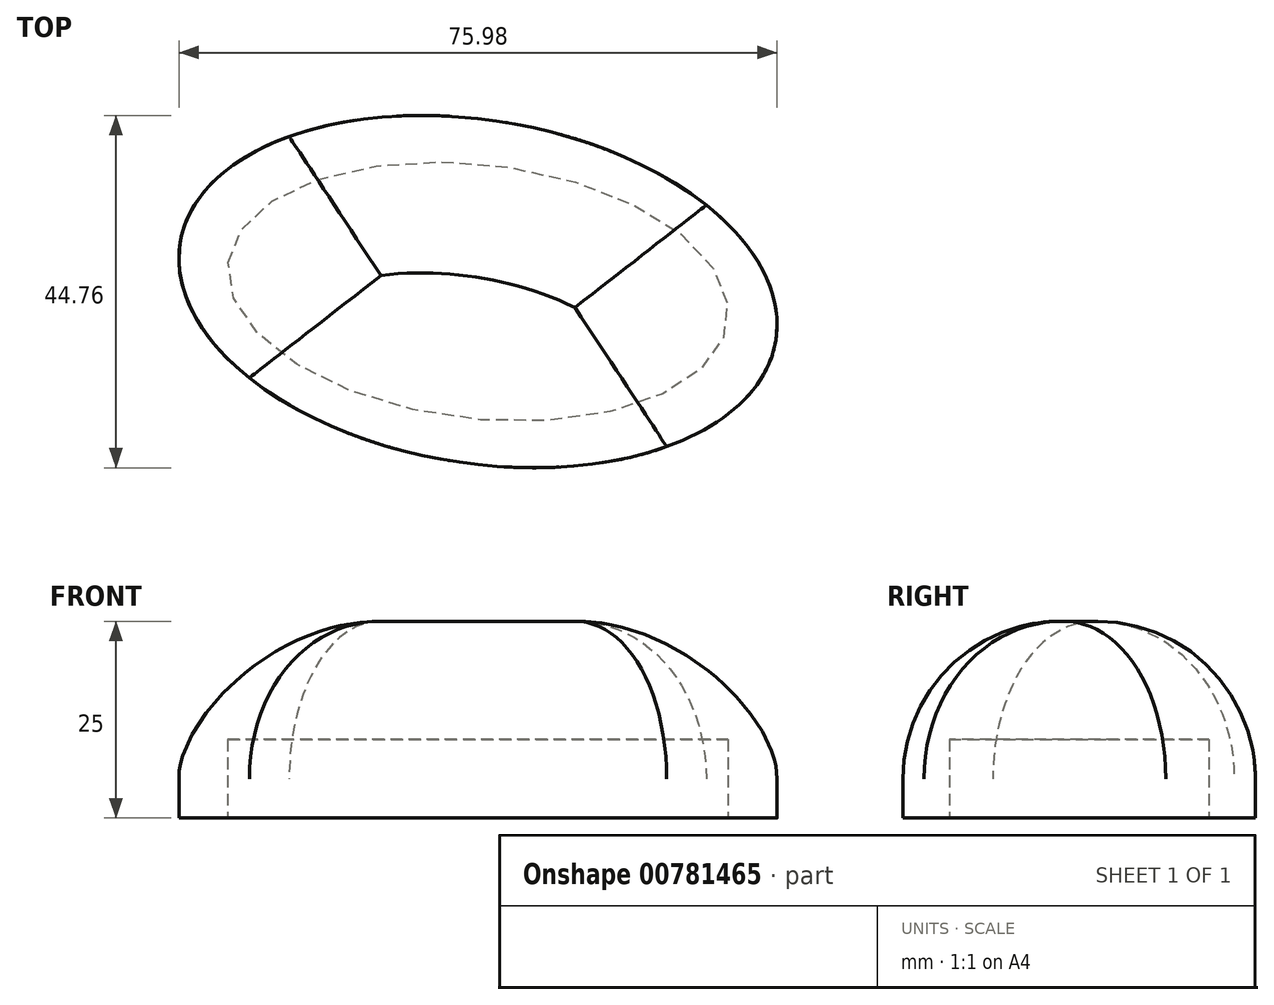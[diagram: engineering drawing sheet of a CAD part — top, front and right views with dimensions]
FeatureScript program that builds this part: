
annotation { "Feature Type Name" : "Feature", "Feature Type Description" : "" }
export const myFeature = defineFeature(function(context is Context, id is Id, definition is map)
    precondition{}
    {
        {
            var Q0;
            Q0=qCreatedBy(makeId("Top.planeOp"),FACE);
            var sketch = newSketch(context, id + "F0", { "sketchPlane" : qUnion([Q0])});
            skLineSegment(sketch, "E0.bottom", {"start": v(44.06, -40.06) * mm, "end": v(-44.06, -40.06) * mm});
            skLineSegment(sketch, "E0.top", {"start": v(44.06, 40.06) * mm, "end": v(-44.06, 40.06) * mm});
            skLineSegment(sketch, "E0.left", {"start": v(44.06, -40.06) * mm, "end": v(44.06, 40.06) * mm});
            skLineSegment(sketch, "E0.right", {"start": v(-44.06, -40.06) * mm, "end": v(-44.06, 40.06) * mm});
            skPoint(sketch, "E0.middle", {"position": v(0, 0) * mm});
            skEllipse(sketch, "E1", {"center": v(0, 0) * mm, "majorRadius": 38.34 * mm, "minorRadius": 21.78 * mm, "majorAxis": v(0.99, -0.16)});
            skSolve(sketch);
        }
        {
            var Q0;
            Q0=makeQuery(id+"F0.imprint","IMPRINT",FACE,{"disambiguationData":[TD([[makeQuery(id+"F0.imprint","IMPRINT",EDGE,{"derivedFrom":sQuery(id+"F0.wireOp",EDGE,"E1")}),1.0]])]});
            extrude(context, id + "F1", {"entities" : qUnion([Q0]), "depth" : 25 * mm, "offsetDistance" : 25 * mm});
        }
        {
            var Q0;
            Q0=makeQuery(id+"F1.opExtrude","CAP_EDGE",EDGE,{"disambiguationData":[OSD([sQuery(id+"F0.wireOp",EDGE,"E1")])],"isStart":false});
            fillet(context, id + "F2", {"entities" : qUnion([Q0]), "radius" : 20 * mm, "tangentPropagation" : true, "allowEdgeOverflow" : false});
        }
        {
            var Q0;
            Q0=makeQuery(id+"F1.opExtrude","CAP_FACE",FACE,{"disambiguationData":[OSD([sQuery(id+"F0.wireOp",EDGE,"E1")])],"isStart":true});
            var sketch = newSketch(context, id + "F3", { "sketchPlane" : qUnion([Q0])});
            skEllipse(sketch, "E2", {"center": v(0, 0) * mm, "majorRadius": 31.94 * mm, "minorRadius": 16.18 * mm, "majorAxis": v(-1, -0.12)});
            skSolve(sketch);
        }
        {
            var Q0;
            Q0=makeQuery(id+"F3.imprint","IMPRINT",FACE,{"disambiguationData":[TD([[makeQuery(id+"F3.imprint","IMPRINT",EDGE,{"derivedFrom":sQuery(id+"F3.wireOp",EDGE,"E2")}),1.0]])]});
            extrude(context, id + "F4", {"entities" : qUnion([Q0]), "operationType" : NewBodyOperationType.REMOVE, "oppositeDirection" : true, "depth" : 10 * mm, "offsetDistance" : 25 * mm});
        }
    });
